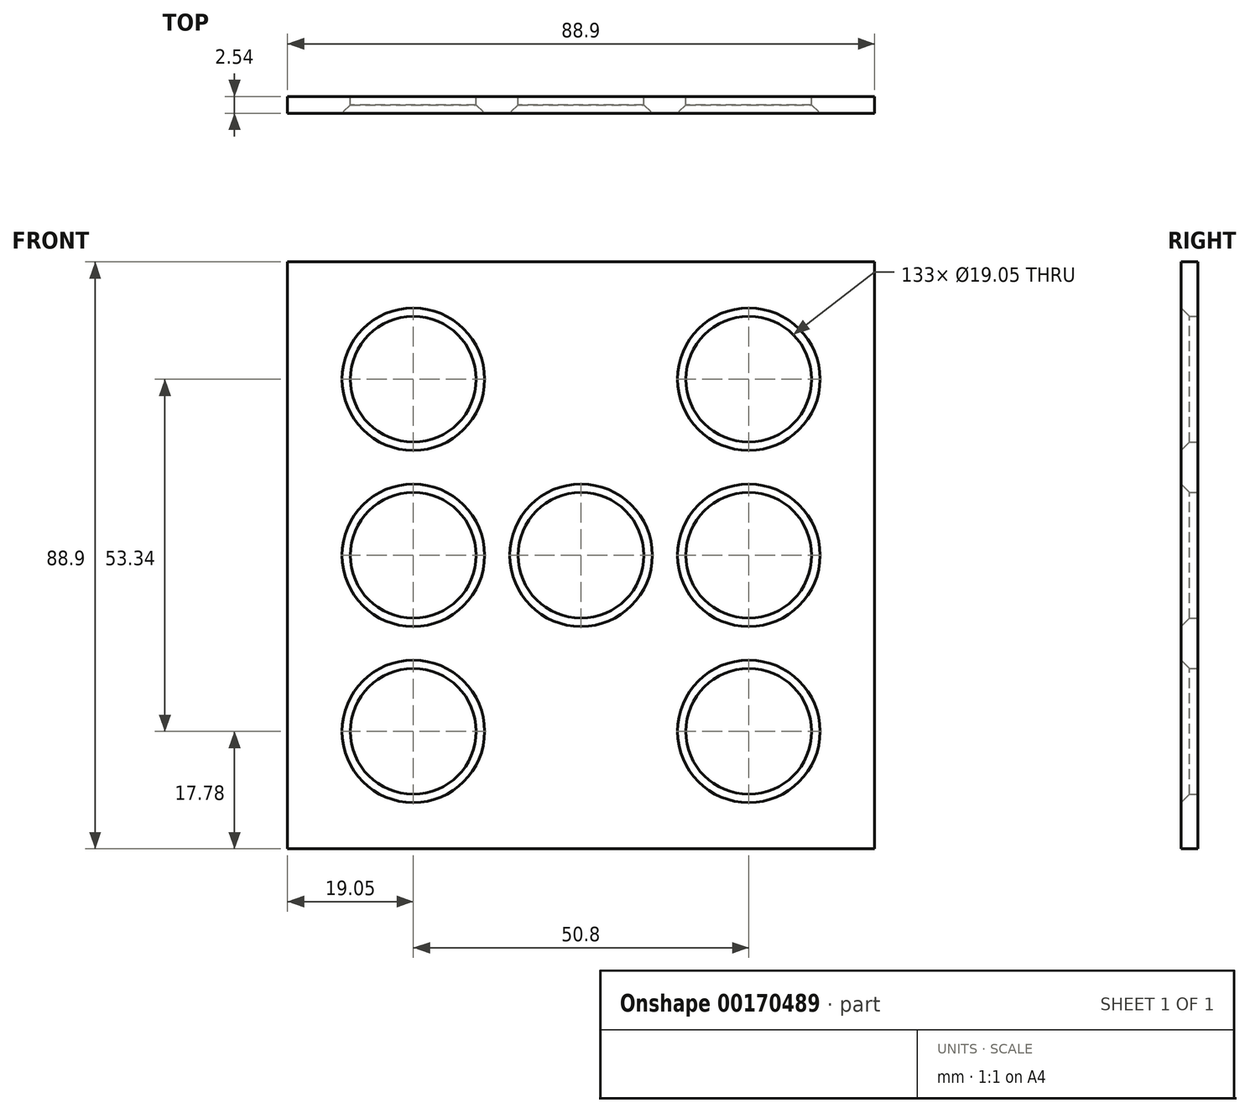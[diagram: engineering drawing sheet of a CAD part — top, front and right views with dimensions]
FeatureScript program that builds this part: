
annotation { "Feature Type Name" : "Feature", "Feature Type Description" : "" }
export const myFeature = defineFeature(function(context is Context, id is Id, definition is map)
    precondition{}
    {
        {
            var Q0;
            Q0=qCreatedBy(makeId("Front.planeOp"),FACE);
            var sketch = newSketch(context, id + "F0", { "sketchPlane" : qUnion([Q0])});
            skLineSegment(sketch, "E0.bottom", {"start": v(-44.45, 44.45) * mm, "end": v(44.45, 44.45) * mm});
            skLineSegment(sketch, "E0.top", {"start": v(-44.45, -44.45) * mm, "end": v(44.45, -44.45) * mm});
            skLineSegment(sketch, "E0.left", {"start": v(-44.45, 44.45) * mm, "end": v(-44.45, -44.45) * mm});
            skLineSegment(sketch, "E0.right", {"start": v(44.45, 44.45) * mm, "end": v(44.45, -44.45) * mm});
            skPoint(sketch, "E0.middle", {"position": v(0, 0) * mm});
            skCircle(sketch, "E1", {"center": v(-25.4, 26.67) * mm, "radius": 9.53 * mm});
            skLineSegment(sketch, "E2.direction1", {"start": v(-25.4, 26.67) * mm, "end": v(0, 26.67) * mm, "construction": true});
            skCircle(sketch, "E3.0.1.0", {"center": v(-25.4, 0) * mm, "radius": 9.53 * mm});
            skCircle(sketch, "E3.0.2.0", {"center": v(-25.4, -26.67) * mm, "radius": 9.53 * mm});
            skCircle(sketch, "E3.1.1.0", {"center": v(0, 0) * mm, "radius": 9.53 * mm});
            skCircle(sketch, "E3.2.0.0", {"center": v(25.4, 26.67) * mm, "radius": 9.53 * mm});
            skCircle(sketch, "E3.2.1.0", {"center": v(25.4, 0) * mm, "radius": 9.53 * mm});
            skCircle(sketch, "E3.2.2.0", {"center": v(25.4, -26.67) * mm, "radius": 9.53 * mm});
            skLineSegment(sketch, "E3.direction2", {"start": v(-25.4, 26.67) * mm, "end": v(-25.4, 0) * mm, "construction": true});
            skSolve(sketch);
        }
        {
            var Q0;
            Q0=makeQuery(id+"F0.imprint","IMPRINT",FACE,{"disambiguationData":[TD([[makeQuery(id+"F0.imprint","IMPRINT",EDGE,{"derivedFrom":sQuery(id+"F0.wireOp",EDGE,"E0.bottom")}),-1.0]])]});
            extrude(context, id + "F1", {"entities" : qUnion([Q0]), "endBound" : BoundingType.SYMMETRIC, "depth" : 2.54 * mm});
        }
        {
            var Q0;
            Q0=makeQuery(id+"F1.opExtrude","CAP_EDGE",EDGE,{"disambiguationData":[OSD([sQuery(id+"F0.wireOp",EDGE,"E1")])],"isStart":false});
            var Q1;
            Q1=makeQuery(id+"F1.opExtrude","CAP_EDGE",EDGE,{"disambiguationData":[OSD([sQuery(id+"F0.wireOp",EDGE,"E3.2.0.0")])],"isStart":false});
            var Q2;
            Q2=makeQuery(id+"F1.opExtrude","CAP_EDGE",EDGE,{"disambiguationData":[OSD([sQuery(id+"F0.wireOp",EDGE,"E3.0.1.0")])],"isStart":false});
            var Q3;
            Q3=makeQuery(id+"F1.opExtrude","CAP_EDGE",EDGE,{"disambiguationData":[OSD([sQuery(id+"F0.wireOp",EDGE,"E3.1.1.0")])],"isStart":false});
            var Q4;
            Q4=makeQuery(id+"F1.opExtrude","CAP_EDGE",EDGE,{"disambiguationData":[OSD([sQuery(id+"F0.wireOp",EDGE,"E3.2.1.0")])],"isStart":false});
            var Q5;
            Q5=makeQuery(id+"F1.opExtrude","CAP_EDGE",EDGE,{"disambiguationData":[OSD([sQuery(id+"F0.wireOp",EDGE,"E3.2.2.0")])],"isStart":false});
            var Q6;
            Q6=makeQuery(id+"F1.opExtrude","CAP_EDGE",EDGE,{"disambiguationData":[OSD([sQuery(id+"F0.wireOp",EDGE,"E3.0.2.0")])],"isStart":false});
            chamfer(context, id + "F2", {"entities" : qUnion([Q0, Q1, Q2, Q3, Q4, Q5, Q6]), "width" : 1.27 * mm, "tangentPropagation" : true});
        }
    });
